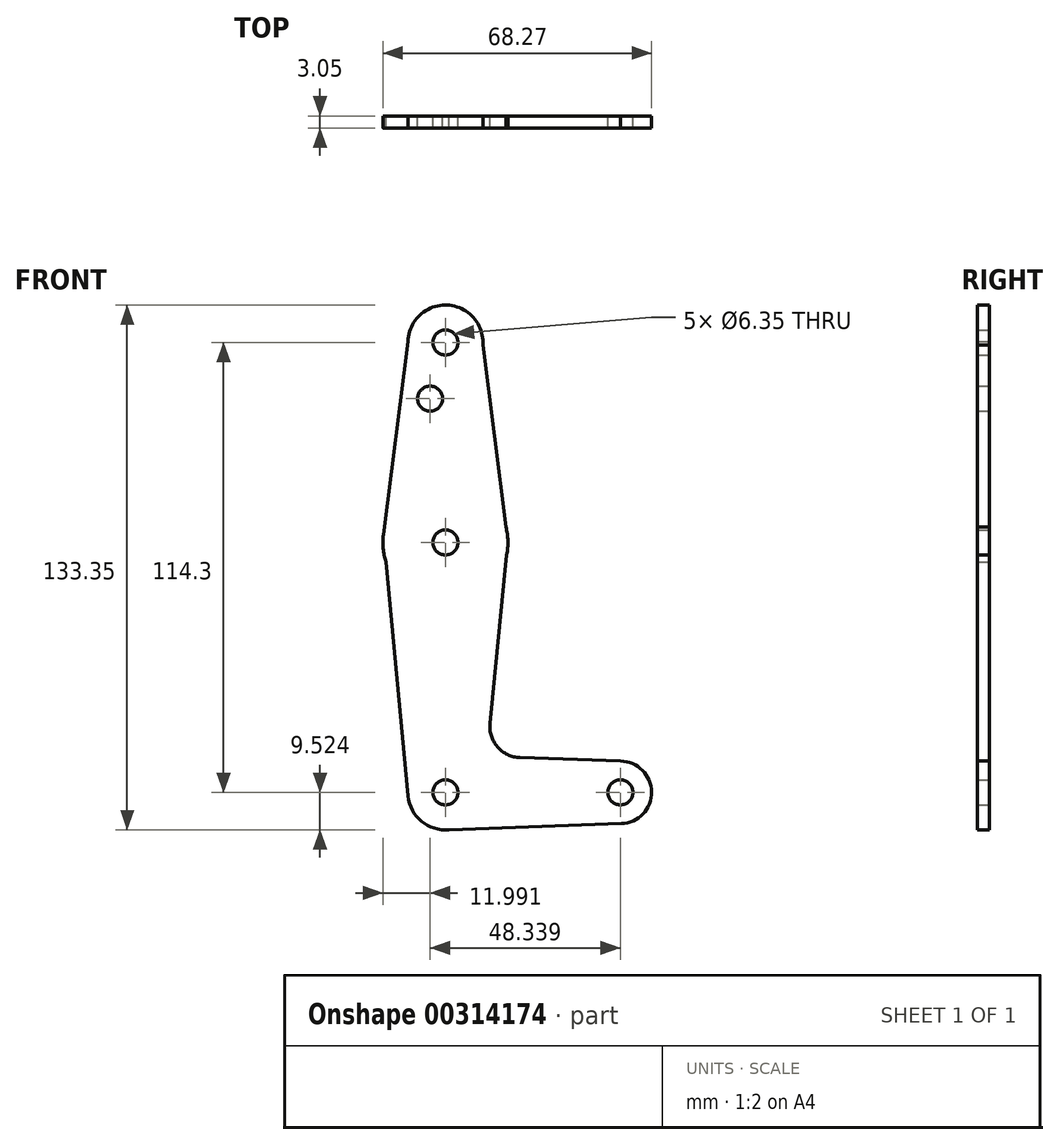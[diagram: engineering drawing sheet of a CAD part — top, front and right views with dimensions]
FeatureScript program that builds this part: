
annotation { "Feature Type Name" : "Feature", "Feature Type Description" : "" }
export const myFeature = defineFeature(function(context is Context, id is Id, definition is map)
    precondition{}
    {
        {
            var Q0;
            Q0=qCreatedBy(makeId("Front.planeOp"),FACE);
            var sketch = newSketch(context, id + "F0", { "sketchPlane" : qUnion([Q0])});
            skCircle(sketch, "E0", {"center": v(0, 103.83) * mm, "radius": 9.53 * mm});
            skCircle(sketch, "E1", {"center": v(0, -10.47) * mm, "radius": 9.52 * mm});
            skCircle(sketch, "E2", {"center": v(0, 53.03) * mm, "radius": 15.88 * mm});
            skCircle(sketch, "E3", {"center": v(44.45, -10.47) * mm, "radius": 7.94 * mm});
            skLineSegment(sketch, "E4", {"start": v(9.03, 106.87) * mm, "end": v(15.88, 53.03) * mm});
            skLineSegment(sketch, "E5", {"start": v(15.88, 53.03) * mm, "end": v(11.32, 7.11) * mm});
            skLineSegment(sketch, "E6", {"start": v(-9.52, 104.1) * mm, "end": v(-15.75, 55.03) * mm});
            skLineSegment(sketch, "E7", {"start": v(-15.75, 55.03) * mm, "end": v(-9.48, -11.36) * mm});
            skLineSegment(sketch, "E8", {"start": v(-0.21, -19.99) * mm, "end": v(44.73, -18.4) * mm});
            skLineSegment(sketch, "E9", {"start": v(44.5, -2.53) * mm, "end": v(18.94, -1.62) * mm});
            skCircle(sketch, "E10", {"center": v(0, 103.83) * mm, "radius": 3.17 * mm});
            skCircle(sketch, "E11", {"center": v(0, 53.03) * mm, "radius": 3.17 * mm});
            skCircle(sketch, "E12", {"center": v(0, -10.47) * mm, "radius": 3.17 * mm});
            skCircle(sketch, "E13", {"center": v(44.45, -10.47) * mm, "radius": 3.18 * mm});
            skLineSegment(sketch, "E14", {"start": v(0, 53.03) * mm, "end": v(0, 89.56) * mm, "construction": true});
            skCircle(sketch, "E15", {"center": v(-3.89, 89.56) * mm, "radius": 3.18 * mm});
            skPoint(sketch, "E16.newPointB", {"position": v(0, -0.94) * mm});
            skArc(sketch, "E16.filletArc", {"start": v(11.32, 7.11) * mm, "mid": v(13.24, 1.1) * mm, "end": v(18.94, -1.62) * mm});
            skSolve(sketch);
        }
        {
            var Q0;
            Q0 = qSketchRegion(id + "F0", true);
            extrude(context, id + "F1", {"entities" : qUnion([Q0]), "depth" : 3.05 * mm});
        }
    });
